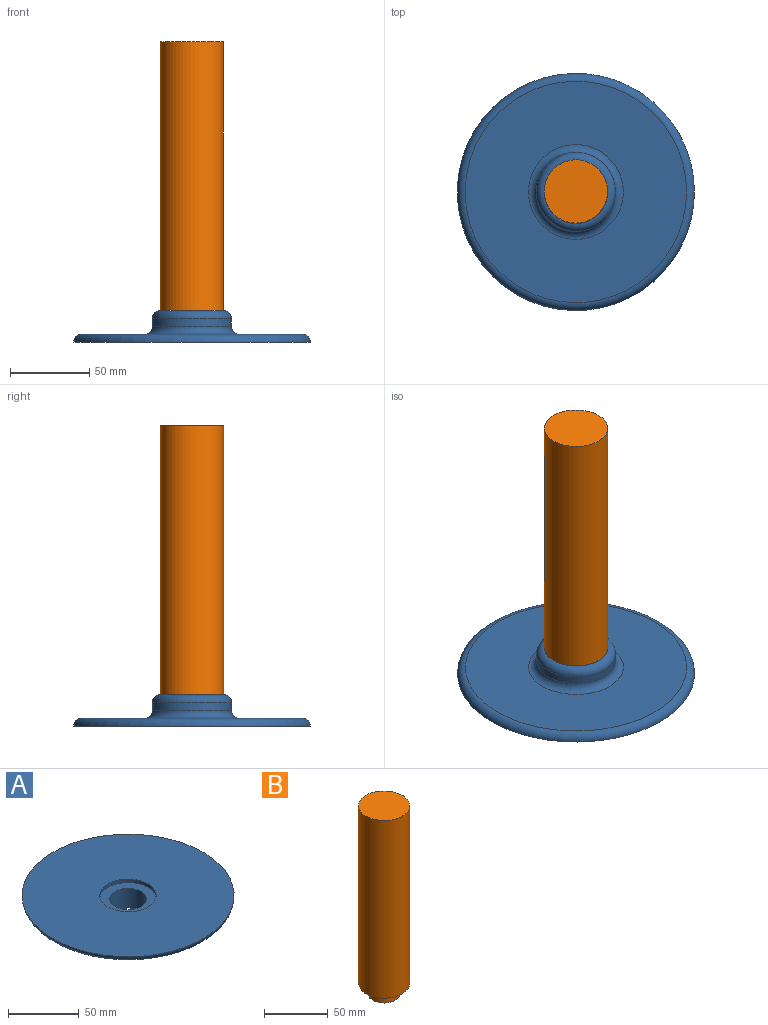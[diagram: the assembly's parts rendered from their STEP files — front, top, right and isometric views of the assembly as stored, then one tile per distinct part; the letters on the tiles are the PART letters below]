
ASSEMBLY  parts=2 mates=1
PART A: 10 faces, bbox 162.4x162.4x23.6 mm
  f0: plane 150x150mm, normal (0,0,1), area 16414.8mm2, adj f2,f8
  f1: plane 140x140mm, normal (0,0,-1), area 12566.4mm2, adj f6,f8
  f2: cylinder r=20mm len=40mm, axis (0,0,1), area 377mm2, adj f0,f3
  f3: plane 40x40mm, normal (0,0,1), area 725.7mm2, adj f2,f9
  f4: cylinder r=25mm len=50mm, axis (0,0,1), area 785.4mm2, adj f6,f7
  f5: plane 40x40mm, normal (0,0,-1), area 725.7mm2, adj f7,f9
  f6: torus R=30mm, axis (0,0,1), area 1323.4mm2, adj f1,f4
  f7: torus R=20mm, axis (0,0,-1), area 1144mm2, adj f4,f5
  f8: torus R=70mm, axis (0,0,1), area 3611.4mm2, adj f0,f1
  f9: cylinder r=13mm len=26mm, axis (0,0,-1), area 1388.6mm2, adj f3,f5
PART B: 5 faces, bbox 40x40x180 mm
  f0: cylinder r=12.5mm len=25mm, axis (0,0,-1), area 785.4mm2, adj f1,f4
  f1: plane 25x25mm, normal (0,0,-1), area 490.9mm2, adj f0
  f2: cylinder r=20mm len=170mm, axis (0,0,-1), area 21362.8mm2, adj f3,f4
  f3: plane 40x40mm, normal (0,0,1), area 1256.6mm2, adj f2
  f4: plane 40x40mm, normal (0,0,-1), area 765.8mm2, adj f0,f2
PLACE A rot(axis=(1,0,0),180deg) t=(0,0,-5.1)mm
PLACE B at identity
MATE fastened A.f4 <-> B.f2  axis (0,0,1) through (0,0,9.9)mm
